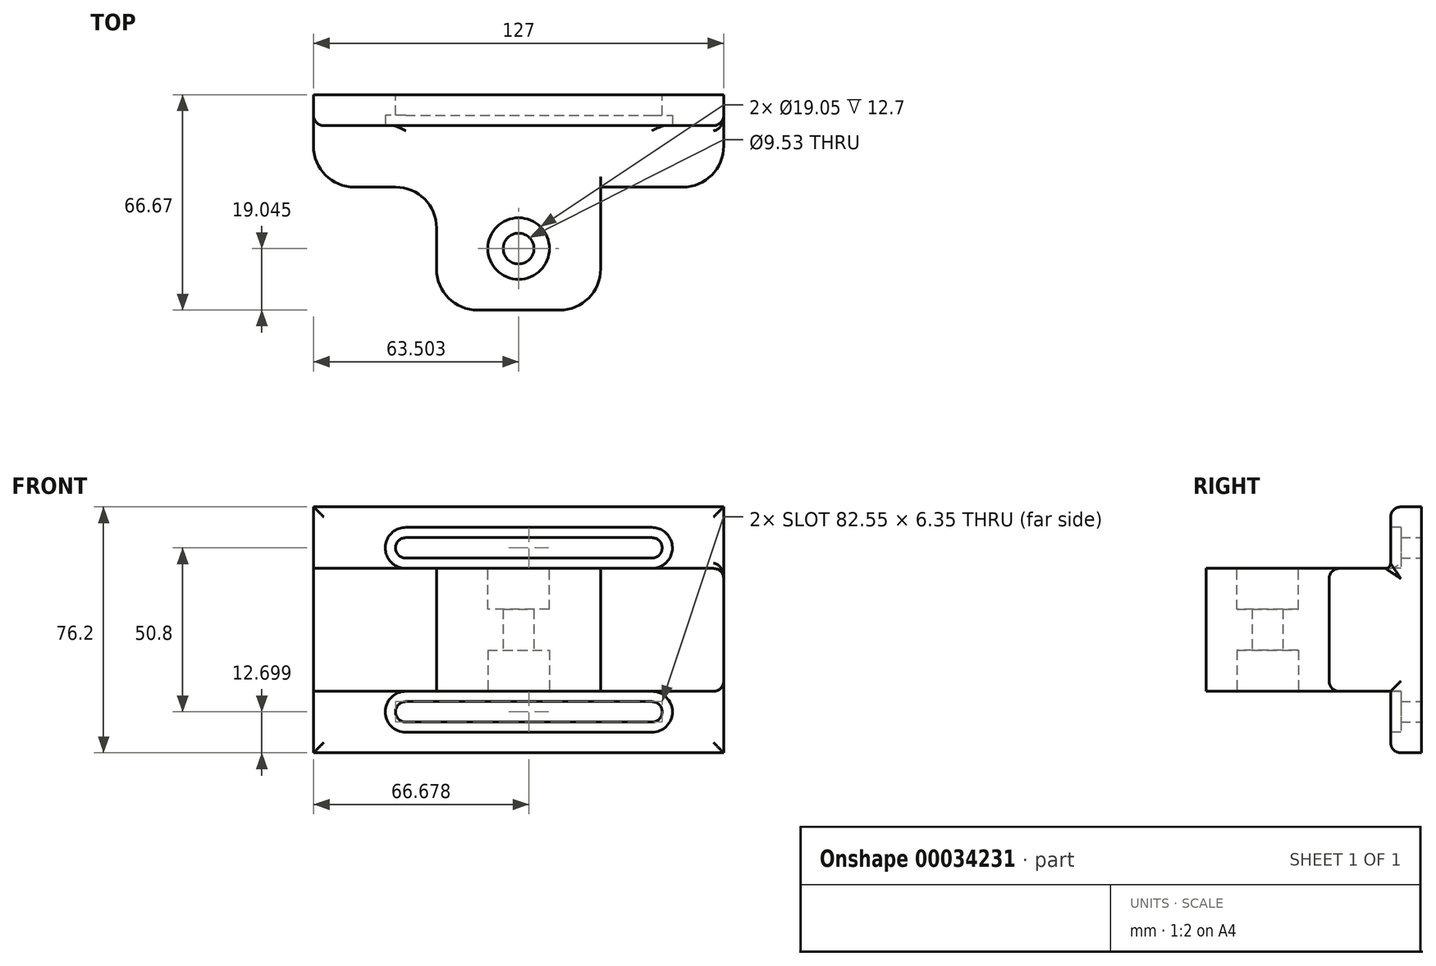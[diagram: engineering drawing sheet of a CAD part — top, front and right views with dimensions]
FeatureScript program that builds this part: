
annotation { "Feature Type Name" : "Feature", "Feature Type Description" : "" }
export const myFeature = defineFeature(function(context is Context, id is Id, definition is map)
    precondition{}
    {
        {
            var Q0;
            Q0=qCreatedBy(makeId("Front.planeOp"),FACE);
            var sketch = newSketch(context, id + "F0", { "sketchPlane" : qUnion([Q0])});
            skLineSegment(sketch, "E0.bottom", {"start": v(-63.03, -41.2) * mm, "end": v(63.97, -41.2) * mm});
            skLineSegment(sketch, "E0.top", {"start": v(-63.03, 35) * mm, "end": v(63.97, 35) * mm});
            skLineSegment(sketch, "E0.left", {"start": v(-63.03, -41.2) * mm, "end": v(-63.03, 35) * mm});
            skLineSegment(sketch, "E0.right", {"start": v(63.97, -41.2) * mm, "end": v(63.97, 35) * mm});
            skArc(sketch, "E1", {"start": v(-34.45, -25.33) * mm, "mid": v(-37.63, -28.5) * mm, "end": v(-34.45, -31.68) * mm});
            skArc(sketch, "E2", {"start": v(41.75, -31.68) * mm, "mid": v(44.92, -28.5) * mm, "end": v(41.75, -25.33) * mm});
            skLineSegment(sketch, "E3", {"start": v(-34.45, -25.33) * mm, "end": v(41.75, -25.33) * mm});
            skLineSegment(sketch, "E4", {"start": v(-34.45, -31.68) * mm, "end": v(41.75, -31.68) * mm});
            skLineSegment(sketch, "E5", {"start": v(-63.03, -3.1) * mm, "end": v(63.97, -3.1) * mm, "construction": true});
            skLineSegment(sketch, "E6.MirrorCS", {"start": v(-34.45, 19.12) * mm, "end": v(41.75, 19.12) * mm});
            skArc(sketch, "E7.MirrorCS", {"start": v(-34.45, 19.12) * mm, "mid": v(-37.63, 22.3) * mm, "end": v(-34.45, 25.47) * mm});
            skLineSegment(sketch, "E8.MirrorCS", {"start": v(-34.45, 25.47) * mm, "end": v(41.75, 25.47) * mm});
            skArc(sketch, "E9.MirrorCS", {"start": v(41.75, 25.47) * mm, "mid": v(44.92, 22.3) * mm, "end": v(41.75, 19.12) * mm});
            skSolve(sketch);
        }
        {
            var Q0;
            Q0=makeQuery(id+"F0.imprint","IMPRINT",FACE,{"disambiguationData":[TD([[makeQuery(id+"F0.imprint","IMPRINT",EDGE,{"derivedFrom":sQuery(id+"F0.wireOp",EDGE,"E0.bottom")}),1.0]])]});
            extrude(context, id + "F1", {"entities" : qUnion([Q0]), "depth" : 9.52 * mm});
        }
        {
            var Q0;
            Q0=makeQuery(id+"F1.opExtrude","CAP_FACE",FACE,{"disambiguationData":[OSD([sQuery(id+"F0.wireOp",EDGE,"E0.bottom"),sQuery(id+"F0.wireOp",EDGE,"E0.top"),sQuery(id+"F0.wireOp",EDGE,"E0.left"),sQuery(id+"F0.wireOp",EDGE,"E0.right"),sQuery(id+"F0.wireOp",EDGE,"E1"),sQuery(id+"F0.wireOp",EDGE,"E2"),sQuery(id+"F0.wireOp",EDGE,"E3"),sQuery(id+"F0.wireOp",EDGE,"E4"),sQuery(id+"F0.wireOp",EDGE,"E6.MirrorCS"),sQuery(id+"F0.wireOp",EDGE,"E7.MirrorCS"),sQuery(id+"F0.wireOp",EDGE,"E8.MirrorCS"),sQuery(id+"F0.wireOp",EDGE,"E9.MirrorCS")])],"isStart":false});
            var sketch = newSketch(context, id + "F2", { "sketchPlane" : qUnion([Q0])});
            skArc(sketch, "E10", {"start": v(-34.45, -22.15) * mm, "mid": v(-40.8, -28.5) * mm, "end": v(-34.45, -34.85) * mm});
            skArc(sketch, "E11", {"start": v(41.75, -34.85) * mm, "mid": v(48.1, -28.5) * mm, "end": v(41.75, -22.15) * mm});
            skLineSegment(sketch, "E12", {"start": v(-34.45, -22.15) * mm, "end": v(41.75, -22.15) * mm});
            skLineSegment(sketch, "E13", {"start": v(-34.45, -34.85) * mm, "end": v(41.75, -34.85) * mm});
            skLineSegment(sketch, "E14", {"start": v(-63.03, -3.1) * mm, "end": v(63.97, -3.1) * mm, "construction": true});
            skLineSegment(sketch, "E15.MirrorCS", {"start": v(-34.45, 15.95) * mm, "end": v(41.75, 15.95) * mm});
            skArc(sketch, "E16.MirrorCS", {"start": v(-34.45, 15.95) * mm, "mid": v(-40.8, 22.3) * mm, "end": v(-34.45, 28.65) * mm});
            skLineSegment(sketch, "E17.MirrorCS", {"start": v(-34.45, 28.65) * mm, "end": v(41.75, 28.65) * mm});
            skArc(sketch, "E18.MirrorCS", {"start": v(41.75, 28.65) * mm, "mid": v(48.1, 22.3) * mm, "end": v(41.75, 15.95) * mm});
            skSolve(sketch);
        }
        {
            var Q0;
            Q0=makeQuery(id+"F2.imprint","IMPRINT",FACE,{"disambiguationData":[TD([[makeQuery(id+"F2.imprint","IMPRINT",EDGE,{"derivedFrom":sQuery(id+"F2.wireOp",EDGE,"E15.MirrorCS")}),1.0]])]});
            var Q1;
            Q1=makeQuery(id+"F2.imprint","IMPRINT",FACE,{"disambiguationData":[TD([[makeQuery(id+"F2.imprint","IMPRINT",EDGE,{"derivedFrom":sQuery(id+"F2.wireOp",EDGE,"E10")}),1.0]])]});
            extrude(context, id + "F3", {"entities" : qUnion([Q0, Q1]), "operationType" : NewBodyOperationType.REMOVE, "oppositeDirection" : true, "depth" : 3.17 * mm});
        }
        {
            var Q0;
            Q0=makeQuery(id+"F1.opExtrude","CAP_FACE",FACE,{"disambiguationData":[OSD([sQuery(id+"F0.wireOp",EDGE,"E0.bottom"),sQuery(id+"F0.wireOp",EDGE,"E0.top"),sQuery(id+"F0.wireOp",EDGE,"E0.left"),sQuery(id+"F0.wireOp",EDGE,"E0.right"),sQuery(id+"F0.wireOp",EDGE,"E1"),sQuery(id+"F0.wireOp",EDGE,"E2"),sQuery(id+"F0.wireOp",EDGE,"E3"),sQuery(id+"F0.wireOp",EDGE,"E4"),sQuery(id+"F0.wireOp",EDGE,"E6.MirrorCS"),sQuery(id+"F0.wireOp",EDGE,"E7.MirrorCS"),sQuery(id+"F0.wireOp",EDGE,"E8.MirrorCS"),sQuery(id+"F0.wireOp",EDGE,"E9.MirrorCS")])],"isStart":false});
            var sketch = newSketch(context, id + "F4", { "sketchPlane" : qUnion([Q0])});
            skLineSegment(sketch, "E19.bottom", {"start": v(-63.03, -22.15) * mm, "end": v(63.97, -22.15) * mm});
            skLineSegment(sketch, "E19.top", {"start": v(-63.03, 15.95) * mm, "end": v(63.97, 15.95) * mm});
            skLineSegment(sketch, "E19.left", {"start": v(-63.03, -22.15) * mm, "end": v(-63.03, 15.95) * mm});
            skLineSegment(sketch, "E19.right", {"start": v(63.97, -22.15) * mm, "end": v(63.97, 15.95) * mm});
            skSolve(sketch);
        }
        {
            var Q0;
            {var subQ1=sQuery(id+"F4.wireOp",EDGE,"E19.left");Q0=makeQuery(id+"F4.imprint","IMPRINT",FACE,{"disambiguationData":[TD([[makeQuery(id+"F4.imprint","IMPRINT",EDGE,{"derivedFrom":subQ1}),-1.0]])]});}
            extrude(context, id + "F5", {"entities" : qUnion([Q0]), "operationType" : NewBodyOperationType.ADD, "depth" : 19.05 * mm});
        }
        {
            var Q0;
            Q0=makeQuery(id+"F5.opExtrude","CAP_FACE",FACE,{"disambiguationData":[OSD([sQuery(id+"F4.wireOp",EDGE,"E19.bottom"),sQuery(id+"F4.wireOp",EDGE,"E19.top"),sQuery(id+"F4.wireOp",EDGE,"E19.left"),sQuery(id+"F4.wireOp",EDGE,"E19.right")])],"isStart":false});
            var sketch = newSketch(context, id + "F6", { "sketchPlane" : qUnion([Q0])});
            skLineSegment(sketch, "E20.bottom", {"start": v(-24.93, -22.15) * mm, "end": v(25.87, -22.15) * mm});
            skLineSegment(sketch, "E20.top", {"start": v(-24.93, 15.95) * mm, "end": v(25.87, 15.95) * mm});
            skLineSegment(sketch, "E20.left", {"start": v(-24.93, -22.15) * mm, "end": v(-24.93, 15.95) * mm});
            skLineSegment(sketch, "E20.right", {"start": v(25.87, -22.15) * mm, "end": v(25.87, 15.95) * mm});
            skSolve(sketch);
        }
        {
            var Q0;
            Q0=makeQuery(id+"F6.imprint","IMPRINT",FACE,{"disambiguationData":[TD([[makeQuery(id+"F6.imprint","IMPRINT",EDGE,{"derivedFrom":sQuery(id+"F6.wireOp",EDGE,"E20.bottom")}),1.0]])]});
            extrude(context, id + "F7", {"entities" : qUnion([Q0]), "operationType" : NewBodyOperationType.ADD, "depth" : 38.1 * mm});
        }
        {
            var Q0;
            Q0=makeQuery(id+"F7.boolean.opBoolean","MERGE",FACE,{"derivedFrom":[makeQuery(id+"F5.boolean.opBoolean","MERGE",FACE,{"derivedFrom":[makeQuery(id+"F3.boolean.opBoolean","COPY",FACE,{"derivedFrom":makeQuery(id+"F3.opExtrude","SWEPT_FACE",FACE,{"disambiguationData":[OSD([sQuery(id+"F2.wireOp",EDGE,"E12")])]})}),makeQuery(id+"F5.opExtrude","SWEPT_FACE",FACE,{"disambiguationData":[OSD([sQuery(id+"F4.wireOp",EDGE,"E19.bottom")])]})]}),makeQuery(id+"F7.opExtrude","SWEPT_FACE",FACE,{"disambiguationData":[OSD([sQuery(id+"F6.wireOp",EDGE,"E20.bottom")])]})]});
            var sketch = newSketch(context, id + "F8", { "sketchPlane" : qUnion([Q0])});
            skPoint(sketch, "E21", {"position": v(0.47, 47.63) * mm});
            skSolve(sketch);
        }
        {
            var Q0;
            Q0=sQuery(id+"F8.wireOp",VERTEX,"E21");
            var Q1;
            Q1=makeQuery(id+"F1.opExtrude","SWEPT_BODY",BODY,{"disambiguationData":[OSD([sQuery(id+"F0.wireOp",EDGE,"E0.bottom"),sQuery(id+"F0.wireOp",EDGE,"E0.top"),sQuery(id+"F0.wireOp",EDGE,"E0.left"),sQuery(id+"F0.wireOp",EDGE,"E0.right"),sQuery(id+"F0.wireOp",EDGE,"E1"),sQuery(id+"F0.wireOp",EDGE,"E2"),sQuery(id+"F0.wireOp",EDGE,"E3"),sQuery(id+"F0.wireOp",EDGE,"E4"),sQuery(id+"F0.wireOp",EDGE,"E6.MirrorCS"),sQuery(id+"F0.wireOp",EDGE,"E7.MirrorCS"),sQuery(id+"F0.wireOp",EDGE,"E8.MirrorCS"),sQuery(id+"F0.wireOp",EDGE,"E9.MirrorCS")])]});
            hole(context, id + "F9", {"style" : HoleStyle.C_BORE, "holeDiameter" : 9.52 * mm, "cBoreDiameter" : 19.05 * mm, "cBoreDepth" : 12.7 * mm, "endStyle" : HoleEndStyle.THROUGH, "locations" : qUnion([Q0]), "scope" : qUnion([Q1])});
        }
        {
            var Q0;
            Q0=makeQuery(id+"F7.boolean.opBoolean","MERGE",FACE,{"derivedFrom":[makeQuery(id+"F5.boolean.opBoolean","MERGE",FACE,{"derivedFrom":[makeQuery(id+"F3.boolean.opBoolean","COPY",FACE,{"derivedFrom":makeQuery(id+"F3.opExtrude","SWEPT_FACE",FACE,{"disambiguationData":[OSD([sQuery(id+"F2.wireOp",EDGE,"E15.MirrorCS")])]})}),makeQuery(id+"F5.opExtrude","SWEPT_FACE",FACE,{"disambiguationData":[OSD([sQuery(id+"F4.wireOp",EDGE,"E19.top")])]})]}),makeQuery(id+"F7.opExtrude","SWEPT_FACE",FACE,{"disambiguationData":[OSD([sQuery(id+"F6.wireOp",EDGE,"E20.top")])]})]});
            var sketch = newSketch(context, id + "F10", { "sketchPlane" : qUnion([Q0])});
            skCircle(sketch, "E22.0", {"center": v(0.47, -47.63) * mm, "radius": 9.52 * mm});
            skSolve(sketch);
        }
        {
            var Q0;
            Q0=makeQuery(id+"F10.imprint","IMPRINT",FACE,{"disambiguationData":[TD([[makeQuery(id+"F10.imprint","IMPRINT",EDGE,{"derivedFrom":sQuery(id+"F10.wireOp",EDGE,"E22.0")}),1.0]])]});
            extrude(context, id + "F11", {"entities" : qUnion([Q0]), "operationType" : NewBodyOperationType.REMOVE, "oppositeDirection" : true, "depth" : 12.7 * mm});
        }
        {
            var Q0;
            Q0=makeQuery(id+"F7.opExtrude","CAP_EDGE",EDGE,{"disambiguationData":[OSD([sQuery(id+"F6.wireOp",EDGE,"E20.left")])],"isStart":false});
            var Q1;
            Q1=makeQuery(id+"F7.opExtrude","CAP_EDGE",EDGE,{"disambiguationData":[OSD([sQuery(id+"F6.wireOp",EDGE,"E20.right")])],"isStart":false});
            var Q2;
            Q2=makeQuery(id+"F5.opExtrude","CAP_EDGE",EDGE,{"disambiguationData":[OSD([sQuery(id+"F4.wireOp",EDGE,"E19.left")])],"isStart":false});
            var Q3;
            Q3=makeQuery(id+"F7.opExtrude","CAP_EDGE",EDGE,{"disambiguationData":[OSD([sQuery(id+"F6.wireOp",EDGE,"E20.left")])],"isStart":true});
            var Q4;
            Q4=makeQuery(id+"F7.opExtrude","CAP_EDGE",EDGE,{"disambiguationData":[OSD([sQuery(id+"F6.wireOp",EDGE,"E20.right")])],"isStart":true});
            var Q5;
            Q5=makeQuery(id+"F5.opExtrude","CAP_EDGE",EDGE,{"disambiguationData":[OSD([sQuery(id+"F4.wireOp",EDGE,"E19.right")])],"isStart":false});
            fillet(context, id + "F12", {"entities" : qUnion([Q0, Q1, Q2, Q3, Q4, Q5]), "radius" : 12.7 * mm, "tangentPropagation" : true, "allowEdgeOverflow" : false});
        }
        {
            var Q0;
            Q0=makeQuery(id+"F1.opExtrude","CAP_EDGE",EDGE,{"disambiguationData":[OSD([sQuery(id+"F0.wireOp",EDGE,"E0.bottom")])],"isStart":false});
            var Q1;
            Q1=makeQuery(id+"F5.opExtrude","SWEPT_EDGE",EDGE,{"disambiguationData":[OSD([sQuery(id+"F0.wireOp",EDGE,"E0.right"),sQuery(id+"F4.wireOp",EDGE,"E19.bottom"),sQuery(id+"F4.wireOp",EDGE,"E19.right")])]});
            var Q2;
            Q2=makeQuery(id+"F12.opFillet","BLEND_EDGE",EDGE,{"blendedFrom":[makeQuery(id+"F5.opExtrude","CAP_EDGE",EDGE,{"disambiguationData":[OSD([sQuery(id+"F4.wireOp",EDGE,"E19.right")])],"isStart":false}),makeQuery(id+"F7.boolean.opBoolean","MERGE",FACE,{"derivedFrom":[makeQuery(id+"F5.boolean.opBoolean","MERGE",FACE,{"derivedFrom":[makeQuery(id+"F3.boolean.opBoolean","COPY",FACE,{"derivedFrom":makeQuery(id+"F3.opExtrude","SWEPT_FACE",FACE,{"disambiguationData":[OSD([sQuery(id+"F2.wireOp",EDGE,"E12")])]})}),makeQuery(id+"F5.opExtrude","SWEPT_FACE",FACE,{"disambiguationData":[OSD([sQuery(id+"F4.wireOp",EDGE,"E19.bottom")])]})]}),makeQuery(id+"F7.opExtrude","SWEPT_FACE",FACE,{"disambiguationData":[OSD([sQuery(id+"F6.wireOp",EDGE,"E20.bottom")])]})]})],"blendedInto":[makeQuery(id+"F7.boolean.opBoolean","MERGE",FACE,{"derivedFrom":[makeQuery(id+"F5.boolean.opBoolean","MERGE",FACE,{"derivedFrom":[makeQuery(id+"F3.boolean.opBoolean","COPY",FACE,{"derivedFrom":makeQuery(id+"F3.opExtrude","SWEPT_FACE",FACE,{"disambiguationData":[OSD([sQuery(id+"F2.wireOp",EDGE,"E12")])]})}),makeQuery(id+"F5.opExtrude","SWEPT_FACE",FACE,{"disambiguationData":[OSD([sQuery(id+"F4.wireOp",EDGE,"E19.bottom")])]})]}),makeQuery(id+"F7.opExtrude","SWEPT_FACE",FACE,{"disambiguationData":[OSD([sQuery(id+"F6.wireOp",EDGE,"E20.bottom")])]})]})]});
            var Q3;
            {var subQ0=sQuery(id+"F4.wireOp",EDGE,"E19.bottom");Q3=makeQuery(id+"F7.boolean.opBoolean","SPLIT",EDGE,{"disambiguationData":[TD([makeQuery(id+"F1.opExtrude","SWEPT_FACE",FACE,{"disambiguationData":[OSD([sQuery(id+"F0.wireOp",EDGE,"E0.right")])]})])],"derivedFrom":makeQuery(id+"F5.opExtrude","CAP_EDGE",EDGE,{"disambiguationData":[OSD([subQ0])],"isStart":false})});}
            var Q4;
            Q4=makeQuery(id+"F12.opFillet","BLEND_EDGE",EDGE,{"blendedFrom":[makeQuery(id+"F7.opExtrude","CAP_EDGE",EDGE,{"disambiguationData":[OSD([sQuery(id+"F6.wireOp",EDGE,"E20.right")])],"isStart":true}),makeQuery(id+"F7.boolean.opBoolean","MERGE",FACE,{"derivedFrom":[makeQuery(id+"F5.boolean.opBoolean","MERGE",FACE,{"derivedFrom":[makeQuery(id+"F3.boolean.opBoolean","COPY",FACE,{"derivedFrom":makeQuery(id+"F3.opExtrude","SWEPT_FACE",FACE,{"disambiguationData":[OSD([sQuery(id+"F2.wireOp",EDGE,"E12")])]})}),makeQuery(id+"F5.opExtrude","SWEPT_FACE",FACE,{"disambiguationData":[OSD([sQuery(id+"F4.wireOp",EDGE,"E19.bottom")])]})]}),makeQuery(id+"F7.opExtrude","SWEPT_FACE",FACE,{"disambiguationData":[OSD([sQuery(id+"F6.wireOp",EDGE,"E20.bottom")])]})]})],"blendedInto":[makeQuery(id+"F7.boolean.opBoolean","MERGE",FACE,{"derivedFrom":[makeQuery(id+"F5.boolean.opBoolean","MERGE",FACE,{"derivedFrom":[makeQuery(id+"F3.boolean.opBoolean","COPY",FACE,{"derivedFrom":makeQuery(id+"F3.opExtrude","SWEPT_FACE",FACE,{"disambiguationData":[OSD([sQuery(id+"F2.wireOp",EDGE,"E12")])]})}),makeQuery(id+"F5.opExtrude","SWEPT_FACE",FACE,{"disambiguationData":[OSD([sQuery(id+"F4.wireOp",EDGE,"E19.bottom")])]})]}),makeQuery(id+"F7.opExtrude","SWEPT_FACE",FACE,{"disambiguationData":[OSD([sQuery(id+"F6.wireOp",EDGE,"E20.bottom")])]})]})]});
            var Q5;
            Q5=makeQuery(id+"F1.opExtrude","CAP_EDGE",EDGE,{"disambiguationData":[OSD([sQuery(id+"F0.wireOp",EDGE,"E0.top")])],"isStart":false});
            var Q6;
            Q6=makeQuery(id+"F5.opExtrude","SWEPT_EDGE",EDGE,{"disambiguationData":[OSD([sQuery(id+"F0.wireOp",EDGE,"E0.right"),sQuery(id+"F4.wireOp",EDGE,"E19.top"),sQuery(id+"F4.wireOp",EDGE,"E19.right")])]});
            var Q7;
            Q7=makeQuery(id+"F12.opFillet","BLEND_EDGE",EDGE,{"blendedFrom":[makeQuery(id+"F5.opExtrude","CAP_EDGE",EDGE,{"disambiguationData":[OSD([sQuery(id+"F4.wireOp",EDGE,"E19.right")])],"isStart":false}),makeQuery(id+"F7.boolean.opBoolean","MERGE",FACE,{"derivedFrom":[makeQuery(id+"F5.boolean.opBoolean","MERGE",FACE,{"derivedFrom":[makeQuery(id+"F3.boolean.opBoolean","COPY",FACE,{"derivedFrom":makeQuery(id+"F3.opExtrude","SWEPT_FACE",FACE,{"disambiguationData":[OSD([sQuery(id+"F2.wireOp",EDGE,"E15.MirrorCS")])]})}),makeQuery(id+"F5.opExtrude","SWEPT_FACE",FACE,{"disambiguationData":[OSD([sQuery(id+"F4.wireOp",EDGE,"E19.top")])]})]}),makeQuery(id+"F7.opExtrude","SWEPT_FACE",FACE,{"disambiguationData":[OSD([sQuery(id+"F6.wireOp",EDGE,"E20.top")])]})]})],"blendedInto":[makeQuery(id+"F7.boolean.opBoolean","MERGE",FACE,{"derivedFrom":[makeQuery(id+"F5.boolean.opBoolean","MERGE",FACE,{"derivedFrom":[makeQuery(id+"F3.boolean.opBoolean","COPY",FACE,{"derivedFrom":makeQuery(id+"F3.opExtrude","SWEPT_FACE",FACE,{"disambiguationData":[OSD([sQuery(id+"F2.wireOp",EDGE,"E15.MirrorCS")])]})}),makeQuery(id+"F5.opExtrude","SWEPT_FACE",FACE,{"disambiguationData":[OSD([sQuery(id+"F4.wireOp",EDGE,"E19.top")])]})]}),makeQuery(id+"F7.opExtrude","SWEPT_FACE",FACE,{"disambiguationData":[OSD([sQuery(id+"F6.wireOp",EDGE,"E20.top")])]})]})]});
            var Q8;
            Q8=makeQuery(id+"F12.opFillet","BLEND_EDGE",EDGE,{"blendedFrom":[makeQuery(id+"F7.opExtrude","CAP_EDGE",EDGE,{"disambiguationData":[OSD([sQuery(id+"F6.wireOp",EDGE,"E20.right")])],"isStart":true}),makeQuery(id+"F7.boolean.opBoolean","MERGE",FACE,{"derivedFrom":[makeQuery(id+"F5.boolean.opBoolean","MERGE",FACE,{"derivedFrom":[makeQuery(id+"F3.boolean.opBoolean","COPY",FACE,{"derivedFrom":makeQuery(id+"F3.opExtrude","SWEPT_FACE",FACE,{"disambiguationData":[OSD([sQuery(id+"F2.wireOp",EDGE,"E15.MirrorCS")])]})}),makeQuery(id+"F5.opExtrude","SWEPT_FACE",FACE,{"disambiguationData":[OSD([sQuery(id+"F4.wireOp",EDGE,"E19.top")])]})]}),makeQuery(id+"F7.opExtrude","SWEPT_FACE",FACE,{"disambiguationData":[OSD([sQuery(id+"F6.wireOp",EDGE,"E20.top")])]})]})],"blendedInto":[makeQuery(id+"F7.boolean.opBoolean","MERGE",FACE,{"derivedFrom":[makeQuery(id+"F5.boolean.opBoolean","MERGE",FACE,{"derivedFrom":[makeQuery(id+"F3.boolean.opBoolean","COPY",FACE,{"derivedFrom":makeQuery(id+"F3.opExtrude","SWEPT_FACE",FACE,{"disambiguationData":[OSD([sQuery(id+"F2.wireOp",EDGE,"E15.MirrorCS")])]})}),makeQuery(id+"F5.opExtrude","SWEPT_FACE",FACE,{"disambiguationData":[OSD([sQuery(id+"F4.wireOp",EDGE,"E19.top")])]})]}),makeQuery(id+"F7.opExtrude","SWEPT_FACE",FACE,{"disambiguationData":[OSD([sQuery(id+"F6.wireOp",EDGE,"E20.top")])]})]})]});
            var Q9;
            {var subQ0=sQuery(id+"F4.wireOp",EDGE,"E19.top");Q9=makeQuery(id+"F7.boolean.opBoolean","SPLIT",EDGE,{"disambiguationData":[TD([makeQuery(id+"F1.opExtrude","SWEPT_FACE",FACE,{"disambiguationData":[OSD([sQuery(id+"F0.wireOp",EDGE,"E0.right")])]})])],"derivedFrom":makeQuery(id+"F5.opExtrude","CAP_EDGE",EDGE,{"disambiguationData":[OSD([subQ0])],"isStart":false})});}
            var Q10;
            {var subQ0=sQuery(id+"F0.wireOp",EDGE,"E0.left");var subQ1=sQuery(id+"F0.wireOp",EDGE,"E0.bottom");Q10=makeQuery(id+"F5.boolean.opBoolean","SPLIT",EDGE,{"disambiguationData":[TD([makeQuery(id+"F1.opExtrude","SWEPT_FACE",FACE,{"disambiguationData":[OSD([subQ1])]})])],"derivedFrom":makeQuery(id+"F1.opExtrude","CAP_EDGE",EDGE,{"disambiguationData":[OSD([subQ0])],"isStart":false})});}
            var Q11;
            {var subQ0=sQuery(id+"F0.wireOp",EDGE,"E0.left");var subQ1=sQuery(id+"F0.wireOp",EDGE,"E0.top");Q11=makeQuery(id+"F5.boolean.opBoolean","SPLIT",EDGE,{"disambiguationData":[TD([makeQuery(id+"F1.opExtrude","SWEPT_FACE",FACE,{"disambiguationData":[OSD([subQ1])]})])],"derivedFrom":makeQuery(id+"F1.opExtrude","CAP_EDGE",EDGE,{"disambiguationData":[OSD([subQ0])],"isStart":false})});}
            var Q12;
            {var subQ0=sQuery(id+"F0.wireOp",EDGE,"E0.right");var subQ1=sQuery(id+"F0.wireOp",EDGE,"E0.bottom");Q12=makeQuery(id+"F5.boolean.opBoolean","SPLIT",EDGE,{"disambiguationData":[TD([makeQuery(id+"F1.opExtrude","SWEPT_FACE",FACE,{"disambiguationData":[OSD([subQ1])]})])],"derivedFrom":makeQuery(id+"F1.opExtrude","CAP_EDGE",EDGE,{"disambiguationData":[OSD([subQ0])],"isStart":false})});}
            var Q13;
            {var subQ0=sQuery(id+"F0.wireOp",EDGE,"E0.right");var subQ1=sQuery(id+"F0.wireOp",EDGE,"E0.top");Q13=makeQuery(id+"F5.boolean.opBoolean","SPLIT",EDGE,{"disambiguationData":[TD([makeQuery(id+"F1.opExtrude","SWEPT_FACE",FACE,{"disambiguationData":[OSD([subQ1])]})])],"derivedFrom":makeQuery(id+"F1.opExtrude","CAP_EDGE",EDGE,{"disambiguationData":[OSD([subQ0])],"isStart":false})});}
            fillet(context, id + "F13", {"entities" : qUnion([Q0, Q1, Q2, Q3, Q4, Q5, Q6, Q7, Q8, Q9, Q10, Q11, Q12, Q13]), "radius" : 3.17 * mm, "tangentPropagation" : true, "allowEdgeOverflow" : false});
        }
        {
            var Q0;
            {var subQ0=sQuery(id+"F4.wireOp",EDGE,"E19.top");var subQ1=sQuery(id+"F0.wireOp",EDGE,"E0.right");Q0=makeQuery(id+"F5.boolean.opBoolean","SPLIT",EDGE,{"disambiguationData":[TD([makeQuery(id+"F1.opExtrude","SWEPT_FACE",FACE,{"disambiguationData":[OSD([subQ1])]})])],"derivedFrom":makeQuery(id+"F5.opExtrude","CAP_EDGE",EDGE,{"disambiguationData":[OSD([subQ0])],"isStart":true})});}
            var Q1;
            {var subQ0=sQuery(id+"F4.wireOp",EDGE,"E19.top");var subQ1=sQuery(id+"F0.wireOp",EDGE,"E0.left");Q1=makeQuery(id+"F5.boolean.opBoolean","SPLIT",EDGE,{"disambiguationData":[TD([makeQuery(id+"F1.opExtrude","SWEPT_FACE",FACE,{"disambiguationData":[OSD([subQ1])]})])],"derivedFrom":makeQuery(id+"F5.opExtrude","CAP_EDGE",EDGE,{"disambiguationData":[OSD([subQ0])],"isStart":true})});}
            var Q2;
            {var subQ0=sQuery(id+"F4.wireOp",EDGE,"E19.bottom");var subQ1=sQuery(id+"F0.wireOp",EDGE,"E0.right");Q2=makeQuery(id+"F5.boolean.opBoolean","SPLIT",EDGE,{"disambiguationData":[TD([makeQuery(id+"F1.opExtrude","SWEPT_FACE",FACE,{"disambiguationData":[OSD([subQ1])]})])],"derivedFrom":makeQuery(id+"F5.opExtrude","CAP_EDGE",EDGE,{"disambiguationData":[OSD([subQ0])],"isStart":true})});}
            var Q3;
            {var subQ0=sQuery(id+"F4.wireOp",EDGE,"E19.bottom");var subQ1=sQuery(id+"F0.wireOp",EDGE,"E0.left");Q3=makeQuery(id+"F5.boolean.opBoolean","SPLIT",EDGE,{"disambiguationData":[TD([makeQuery(id+"F1.opExtrude","SWEPT_FACE",FACE,{"disambiguationData":[OSD([subQ1])]})])],"derivedFrom":makeQuery(id+"F5.opExtrude","CAP_EDGE",EDGE,{"disambiguationData":[OSD([subQ0])],"isStart":true})});}
            fillet(context, id + "F14", {"entities" : qUnion([Q0, Q1, Q2, Q3]), "radius" : 1.59 * mm, "tangentPropagation" : true, "allowEdgeOverflow" : false});
        }
        {
            var Q0;
            Q0=makeQuery(id+"F7.boolean.opBoolean","MERGE",FACE,{"derivedFrom":[makeQuery(id+"F5.boolean.opBoolean","MERGE",FACE,{"derivedFrom":[makeQuery(id+"F3.boolean.opBoolean","COPY",FACE,{"derivedFrom":makeQuery(id+"F3.opExtrude","SWEPT_FACE",FACE,{"disambiguationData":[OSD([sQuery(id+"F2.wireOp",EDGE,"E15.MirrorCS")])]})}),makeQuery(id+"F5.opExtrude","SWEPT_FACE",FACE,{"disambiguationData":[OSD([sQuery(id+"F4.wireOp",EDGE,"E19.top")])]})]}),makeQuery(id+"F7.opExtrude","SWEPT_FACE",FACE,{"disambiguationData":[OSD([sQuery(id+"F6.wireOp",EDGE,"E20.top")])]})]});
            var sketch = newSketch(context, id + "F15", { "sketchPlane" : qUnion([Q0])});
            skCircle(sketch, "E23", {"center": v(0.47, -47.63) * mm, "radius": 12.7 * mm});
            skSolve(sketch);
        }
        {
            var Q0;
            Q0=makeQuery(id+"F15.imprint","IMPRINT",FACE,{"disambiguationData":[TD([[makeQuery(id+"F15.imprint","IMPRINT",EDGE,{"derivedFrom":sQuery(id+"F15.wireOp",EDGE,"E23")}),1.0]])]});
            extrude(context, id + "F16", {"entities" : qUnion([Q0]), "operationType" : NewBodyOperationType.REMOVE, "depth" : 2.54 * mm});
        }
    });
